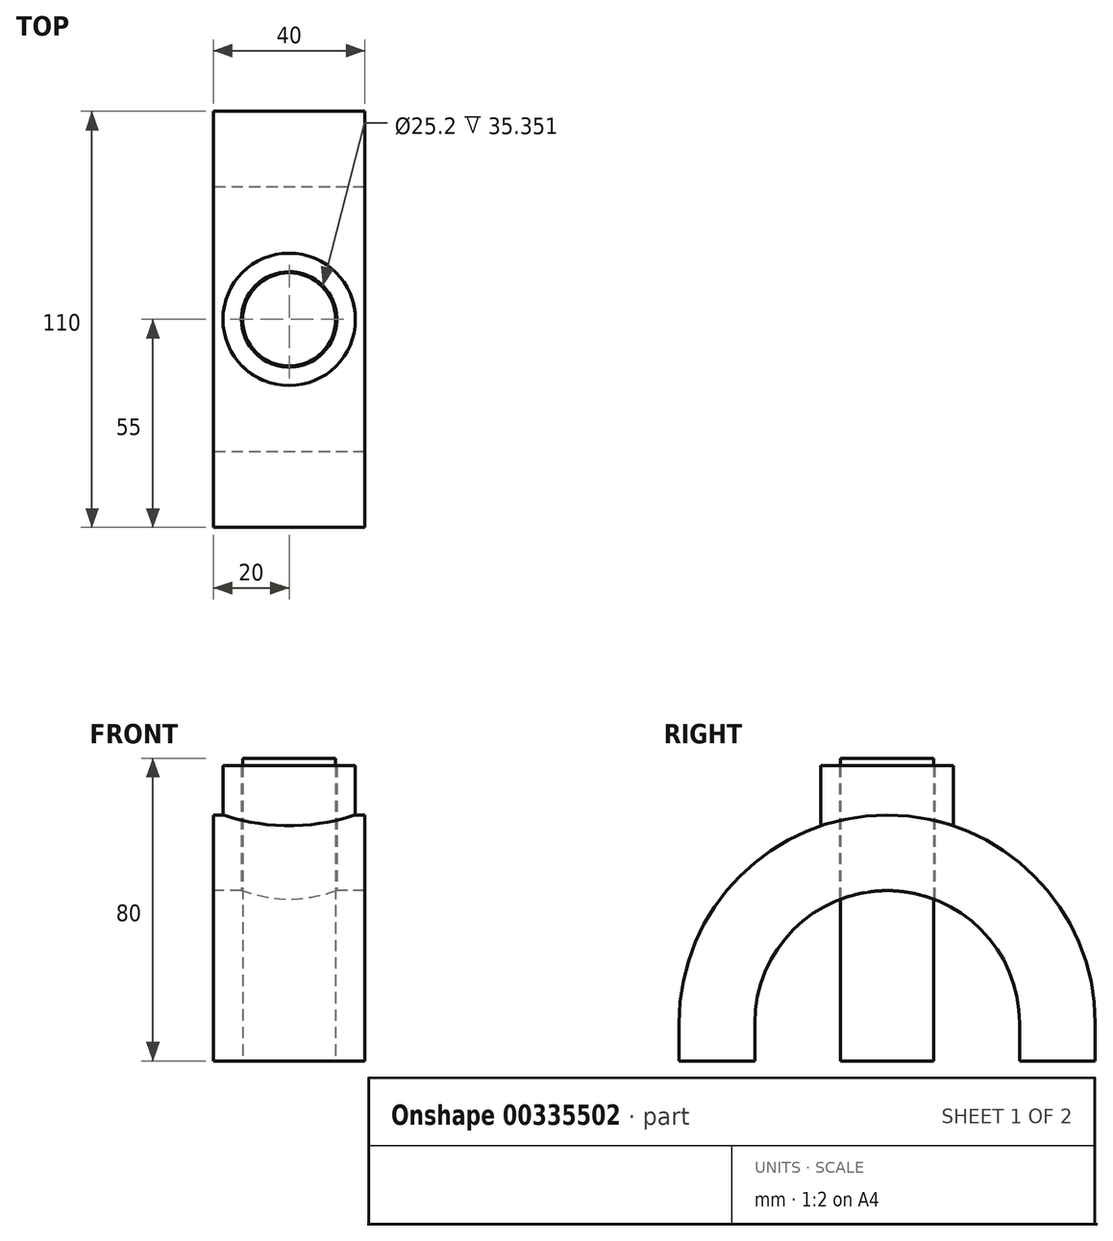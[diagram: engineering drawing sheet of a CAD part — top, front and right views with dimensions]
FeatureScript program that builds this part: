
annotation { "Feature Type Name" : "Feature", "Feature Type Description" : "" }
export const myFeature = defineFeature(function(context is Context, id is Id, definition is map)
    precondition{}
    {
        {
            var Q0;
            Q0=qCreatedBy(makeId("Right.planeOp"),FACE);
            var sketch = newSketch(context, id + "F0", { "sketchPlane" : qUnion([Q0])});
            skLineSegment(sketch, "E0", {"start": v(-35, 0) * mm, "end": v(35, 0) * mm, "construction": true});
            skPoint(sketch, "E1", {"position": v(0, 0) * mm});
            skLineSegment(sketch, "E2.bottom", {"start": v(35, 0) * mm, "end": v(55, 0) * mm});
            skLineSegment(sketch, "E2.top", {"start": v(35, 10) * mm, "end": v(55, 10) * mm});
            skLineSegment(sketch, "E2.left", {"start": v(35, 0) * mm, "end": v(35, 10) * mm});
            skLineSegment(sketch, "E2.right", {"start": v(55, 0) * mm, "end": v(55, 10) * mm});
            skLineSegment(sketch, "E3.bottom", {"start": v(-35, 0) * mm, "end": v(-55, 0) * mm});
            skLineSegment(sketch, "E3.top", {"start": v(-35, 10) * mm, "end": v(-55, 10) * mm});
            skLineSegment(sketch, "E3.left", {"start": v(-35, 0) * mm, "end": v(-35, 10) * mm});
            skLineSegment(sketch, "E3.right", {"start": v(-55, 0) * mm, "end": v(-55, 10) * mm});
            skArc(sketch, "E4", {"start": v(35, 10) * mm, "mid": v(0, 45) * mm, "end": v(-35, 10) * mm});
            skArc(sketch, "E5", {"start": v(55, 10) * mm, "mid": v(0, 65) * mm, "end": v(-55, 10) * mm});
            skSolve(sketch);
        }
        {
            var Q0;
            Q0=makeQuery(id+"F0.imprint","IMPRINT",FACE,{"disambiguationData":[TD([[makeQuery(id+"F0.imprint","IMPRINT",EDGE,{"derivedFrom":sQuery(id+"F0.wireOp",EDGE,"E2.top")}),1.0]])]});
            var Q1;
            Q1=makeQuery(id+"F0.imprint","IMPRINT",FACE,{"disambiguationData":[TD([[makeQuery(id+"F0.imprint","IMPRINT",EDGE,{"derivedFrom":sQuery(id+"F0.wireOp",EDGE,"E3.bottom")}),-1.0]])]});
            var Q2;
            Q2=makeQuery(id+"F0.imprint","IMPRINT",FACE,{"disambiguationData":[TD([[makeQuery(id+"F0.imprint","IMPRINT",EDGE,{"derivedFrom":sQuery(id+"F0.wireOp",EDGE,"E2.bottom")}),1.0]])]});
            extrude(context, id + "F1", {"entities" : qUnion([Q0, Q1, Q2]), "depth" : 20 * mm, "hasSecondDirection" : true, "secondDirectionOppositeDirection" : true, "secondDirectionDepth" : 20 * mm});
        }
        {
            var Q0;
            Q0=qCreatedBy(makeId("Top.planeOp"),FACE);
            cPlane(context, id + "F2", {"entities" : qUnion([Q0]), "cplaneType" : CPlaneType.OFFSET, "offset" : 48 * mm, "width" : 150 * mm, "height" : 150 * mm});
        }
        {
            var Q0;
            Q0=qCreatedBy(id+"F2.planeOp",FACE);
            var sketch = newSketch(context, id + "F3", { "sketchPlane" : qUnion([Q0])});
            skCircle(sketch, "E6", {"center": v(0, 0) * mm, "radius": 12.6 * mm});
            skCircle(sketch, "E7", {"center": v(0, 0) * mm, "radius": 17.5 * mm});
            skSolve(sketch);
        }
        {
            var Q0;
            Q0=makeQuery(id+"F3.imprint","IMPRINT",FACE,{"disambiguationData":[TD([[makeQuery(id+"F3.imprint","IMPRINT",EDGE,{"derivedFrom":sQuery(id+"F3.wireOp",EDGE,"E6")}),-1.0]])]});
            extrude(context, id + "F4", {"entities" : qUnion([Q0]), "operationType" : NewBodyOperationType.ADD, "depth" : 30 * mm});
        }
        {
            var Q0;
            Q0=makeQuery(id+"F3.imprint","IMPRINT",FACE,{"disambiguationData":[TD([[makeQuery(id+"F3.imprint","IMPRINT",EDGE,{"derivedFrom":sQuery(id+"F3.wireOp",EDGE,"E6")}),1.0]])]});
            extrude(context, id + "F5", {"entities" : qUnion([Q0]), "operationType" : NewBodyOperationType.REMOVE, "oppositeDirection" : true, "depth" : 30 * mm, "hasSecondDirection" : true, "secondDirectionOppositeDirection" : false, "secondDirectionDepth" : 40 * mm});
        }
        {
            var Q0;
            Q0=qCreatedBy(makeId("Top.planeOp"),FACE);
            var sketch = newSketch(context, id + "F6", { "sketchPlane" : qUnion([Q0])});
            skCircle(sketch, "E8", {"center": v(0, 0) * mm, "radius": 12.3 * mm});
            skSolve(sketch);
        }
        {
            var Q0;
            Q0=makeQuery(id+"F6.imprint","IMPRINT",FACE,{"disambiguationData":[TD([[makeQuery(id+"F6.imprint","IMPRINT",EDGE,{"derivedFrom":sQuery(id+"F6.wireOp",EDGE,"E8")}),1.0]])]});
            extrude(context, id + "F7", {"entities" : qUnion([Q0]), "depth" : 80 * mm});
        }
    });
